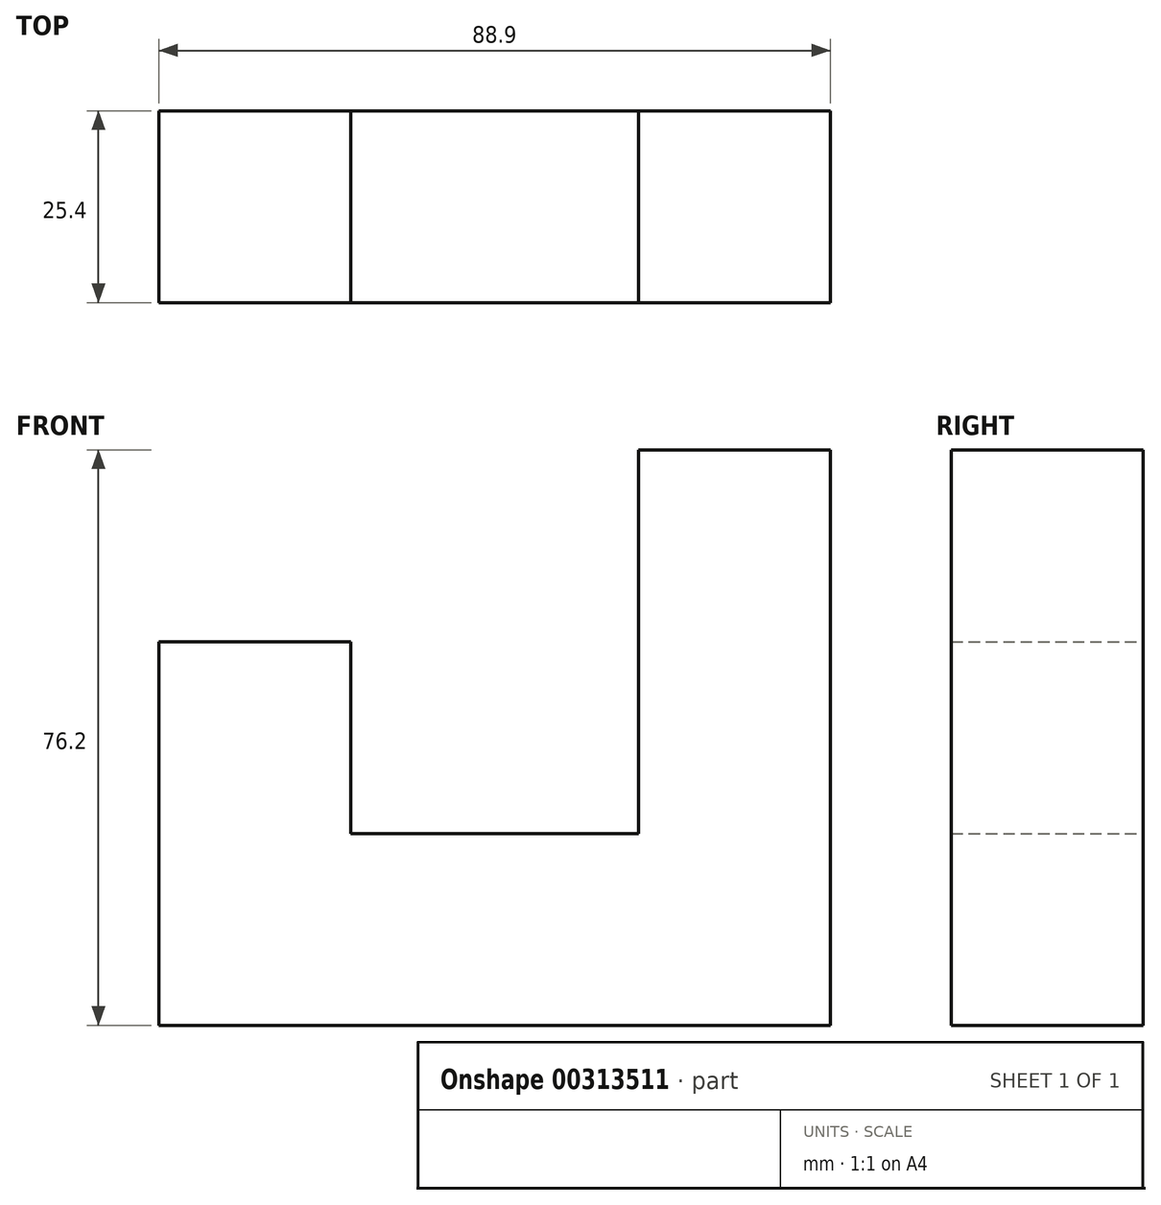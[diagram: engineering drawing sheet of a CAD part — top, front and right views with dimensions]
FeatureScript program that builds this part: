
annotation { "Feature Type Name" : "Feature", "Feature Type Description" : "" }
export const myFeature = defineFeature(function(context is Context, id is Id, definition is map)
    precondition{}
    {
        {
            var Q0;
            Q0=qCreatedBy(makeId("Front.planeOp"),FACE);
            var sketch = newSketch(context, id + "F0", { "sketchPlane" : qUnion([Q0])});
            skLineSegment(sketch, "E0", {"start": v(-43.38, -45.47) * mm, "end": v(45.52, -45.47) * mm});
            skLineSegment(sketch, "E1", {"start": v(45.52, -45.47) * mm, "end": v(45.52, 30.73) * mm});
            skLineSegment(sketch, "E2", {"start": v(45.52, 30.73) * mm, "end": v(20.12, 30.73) * mm});
            skLineSegment(sketch, "E3", {"start": v(20.12, 30.73) * mm, "end": v(20.12, -20.07) * mm});
            skLineSegment(sketch, "E4", {"start": v(20.12, -20.07) * mm, "end": v(-17.98, -20.07) * mm});
            skLineSegment(sketch, "E5", {"start": v(-17.98, -20.07) * mm, "end": v(-17.98, 5.33) * mm});
            skLineSegment(sketch, "E6", {"start": v(-17.98, 5.33) * mm, "end": v(-43.38, 5.33) * mm});
            skLineSegment(sketch, "E7", {"start": v(-43.38, 5.33) * mm, "end": v(-43.38, -45.47) * mm});
            skSolve(sketch);
        }
        {
            var Q0;
            Q0=makeQuery(id+"F0.imprint","IMPRINT",FACE,{"disambiguationData":[TD([[makeQuery(id+"F0.imprint","IMPRINT",EDGE,{"derivedFrom":sQuery(id+"F0.wireOp",EDGE,"E0")}),1.0]])]});
            extrude(context, id + "F1", {"entities" : qUnion([Q0]), "depth" : 25.4 * mm});
        }
    });
